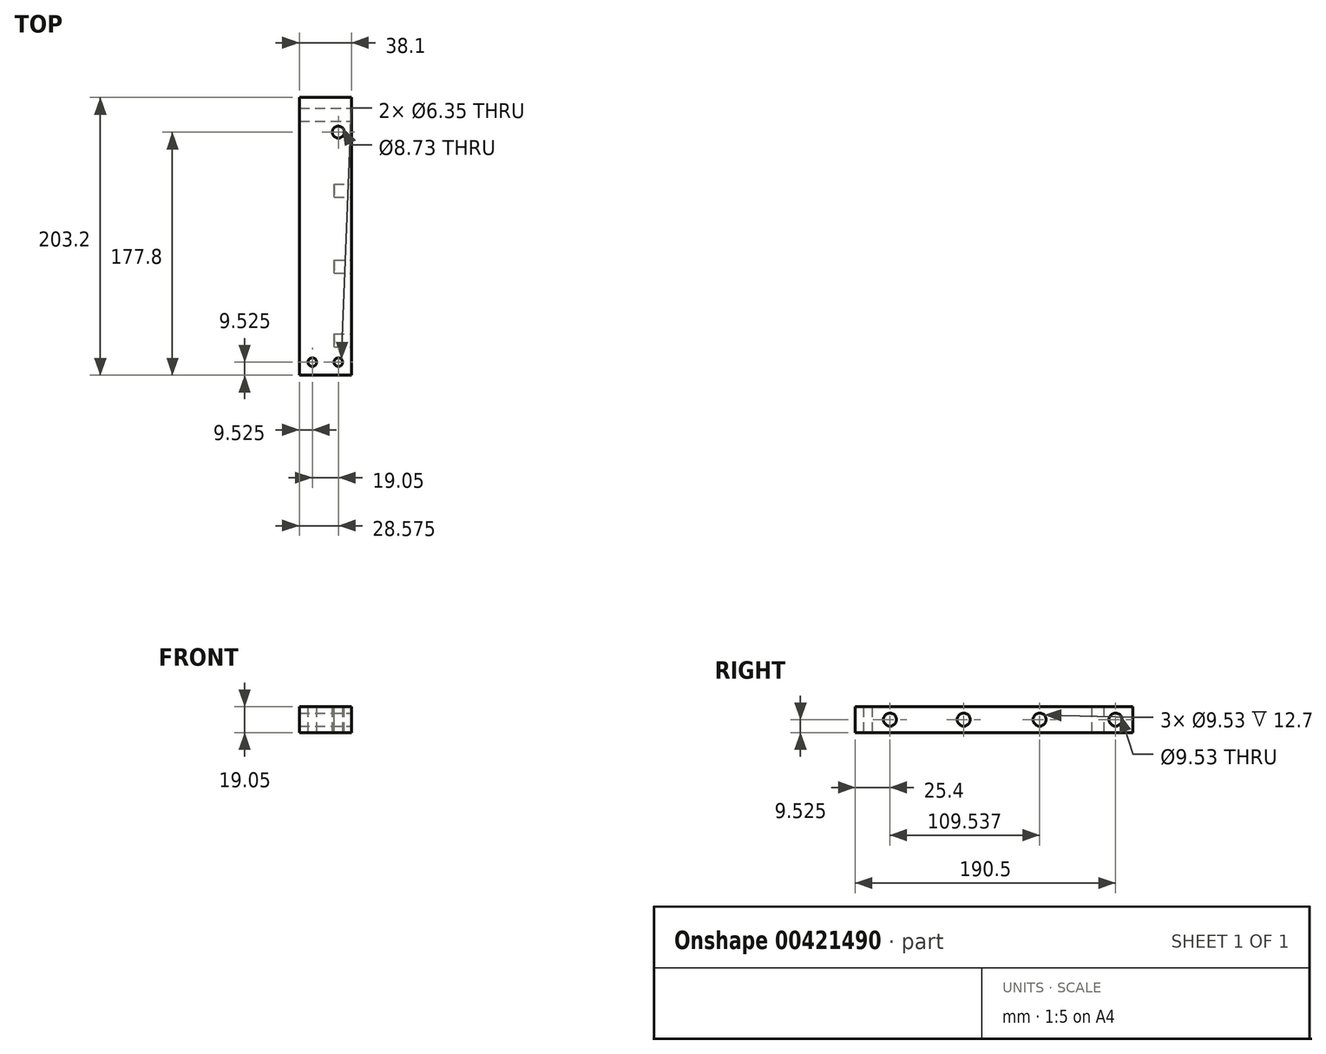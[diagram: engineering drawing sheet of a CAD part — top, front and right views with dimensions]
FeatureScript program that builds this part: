
annotation { "Feature Type Name" : "Feature", "Feature Type Description" : "" }
export const myFeature = defineFeature(function(context is Context, id is Id, definition is map)
    precondition{}
    {
        {
            var Q0;
            Q0=qCreatedBy(makeId("Top.planeOp"),FACE);
            var sketch = newSketch(context, id + "F0", { "sketchPlane" : qUnion([Q0])});
            skLineSegment(sketch, "E0.bottom", {"start": v(19.05, 101.6) * mm, "end": v(-19.05, 101.6) * mm});
            skLineSegment(sketch, "E0.top", {"start": v(19.05, -101.6) * mm, "end": v(-19.05, -101.6) * mm});
            skLineSegment(sketch, "E0.left", {"start": v(19.05, 101.6) * mm, "end": v(19.05, -101.6) * mm});
            skLineSegment(sketch, "E0.right", {"start": v(-19.05, 101.6) * mm, "end": v(-19.05, -101.6) * mm});
            skPoint(sketch, "E0.middle", {"position": v(0, 0) * mm});
            skSolve(sketch);
        }
        {
            var Q0;
            Q0=makeQuery(id+"F0.imprint","IMPRINT",FACE,{"disambiguationData":[TD([[makeQuery(id+"F0.imprint","IMPRINT",EDGE,{"derivedFrom":sQuery(id+"F0.wireOp",EDGE,"E0.bottom")}),1.0]])]});
            extrude(context, id + "F1", {"entities" : qUnion([Q0]), "depth" : 19.05 * mm});
        }
        {
            var Q0;
            Q0=makeQuery(id+"F1.opExtrude","SWEPT_FACE",FACE,{"disambiguationData":[OSD([sQuery(id+"F0.wireOp",EDGE,"E0.left")])]});
            var sketch = newSketch(context, id + "F2", { "sketchPlane" : qUnion([Q0])});
            skLineSegment(sketch, "E1", {"start": v(101.6, 9.53) * mm, "end": v(-101.6, 9.53) * mm, "construction": true});
            skCircle(sketch, "E2", {"center": v(88.9, 9.53) * mm, "radius": 4.76 * mm});
            skCircle(sketch, "E3", {"center": v(-76.2, 9.53) * mm, "radius": 4.76 * mm});
            skCircle(sketch, "E4", {"center": v(33.34, 9.52) * mm, "radius": 4.76 * mm});
            skCircle(sketch, "E5", {"center": v(-22.22, 9.52) * mm, "radius": 4.76 * mm});
            skSolve(sketch);
        }
        {
            var Q0;
            Q0=makeQuery(id+"F2.imprint","IMPRINT",FACE,{"disambiguationData":[TD([[makeQuery(id+"F2.imprint","IMPRINT",EDGE,{"derivedFrom":sQuery(id+"F2.wireOp",EDGE,"E2")}),1.0]])]});
            extrude(context, id + "F3", {"entities" : qUnion([Q0]), "operationType" : NewBodyOperationType.REMOVE, "endBound" : BoundingType.THROUGH_ALL, "oppositeDirection" : true, "depth" : 25.4 * mm});
        }
        {
            var Q0;
            Q0=makeQuery(id+"F1.opExtrude","CAP_FACE",FACE,{"disambiguationData":[OSD([sQuery(id+"F0.wireOp",EDGE,"E0.bottom"),sQuery(id+"F0.wireOp",EDGE,"E0.top"),sQuery(id+"F0.wireOp",EDGE,"E0.left"),sQuery(id+"F0.wireOp",EDGE,"E0.right")])],"isStart":false});
            var sketch = newSketch(context, id + "F4", { "sketchPlane" : qUnion([Q0])});
            skLineSegment(sketch, "E6", {"start": v(-19.05, -92.08) * mm, "end": v(19.05, -92.07) * mm, "construction": true});
            skCircle(sketch, "E7", {"center": v(-9.52, -92.08) * mm, "radius": 3.18 * mm});
            skCircle(sketch, "E8", {"center": v(9.53, -92.08) * mm, "radius": 3.18 * mm});
            skSolve(sketch);
        }
        {
            var Q0;
            Q0 = qSketchRegion(id + "F4", true);
            extrude(context, id + "F5", {"entities" : qUnion([Q0]), "operationType" : NewBodyOperationType.REMOVE, "endBound" : BoundingType.THROUGH_ALL, "oppositeDirection" : true, "depth" : 25.4 * mm});
        }
        {
            var Q0;
            Q0=makeQuery(id+"F1.opExtrude","CAP_FACE",FACE,{"disambiguationData":[OSD([sQuery(id+"F0.wireOp",EDGE,"E0.bottom"),sQuery(id+"F0.wireOp",EDGE,"E0.top"),sQuery(id+"F0.wireOp",EDGE,"E0.left"),sQuery(id+"F0.wireOp",EDGE,"E0.right")])],"isStart":false});
            var sketch = newSketch(context, id + "F6", { "sketchPlane" : qUnion([Q0])});
            skCircle(sketch, "E9", {"center": v(9.52, 76.2) * mm, "radius": 4.37 * mm});
            skSolve(sketch);
        }
        {
            var Q0;
            Q0 = qSketchRegion(id + "F6", true);
            extrude(context, id + "F7", {"entities" : qUnion([Q0]), "operationType" : NewBodyOperationType.REMOVE, "endBound" : BoundingType.THROUGH_ALL, "oppositeDirection" : true, "depth" : 25.4 * mm});
        }
        {
            var Q0;
            Q0=makeQuery(id+"F2.imprint","IMPRINT",FACE,{"disambiguationData":[TD([[makeQuery(id+"F2.imprint","IMPRINT",EDGE,{"derivedFrom":sQuery(id+"F2.wireOp",EDGE,"E4")}),1.0]])]});
            var Q1;
            Q1=makeQuery(id+"F2.imprint","IMPRINT",FACE,{"disambiguationData":[TD([[makeQuery(id+"F2.imprint","IMPRINT",EDGE,{"derivedFrom":sQuery(id+"F2.wireOp",EDGE,"E5")}),1.0]])]});
            var Q2;
            Q2=makeQuery(id+"F2.imprint","IMPRINT",FACE,{"disambiguationData":[TD([[makeQuery(id+"F2.imprint","IMPRINT",EDGE,{"derivedFrom":sQuery(id+"F2.wireOp",EDGE,"E3")}),1.0]])]});
            extrude(context, id + "F8", {"entities" : qUnion([Q0, Q1, Q2]), "operationType" : NewBodyOperationType.REMOVE, "oppositeDirection" : true, "depth" : 12.7 * mm});
        }
    });
